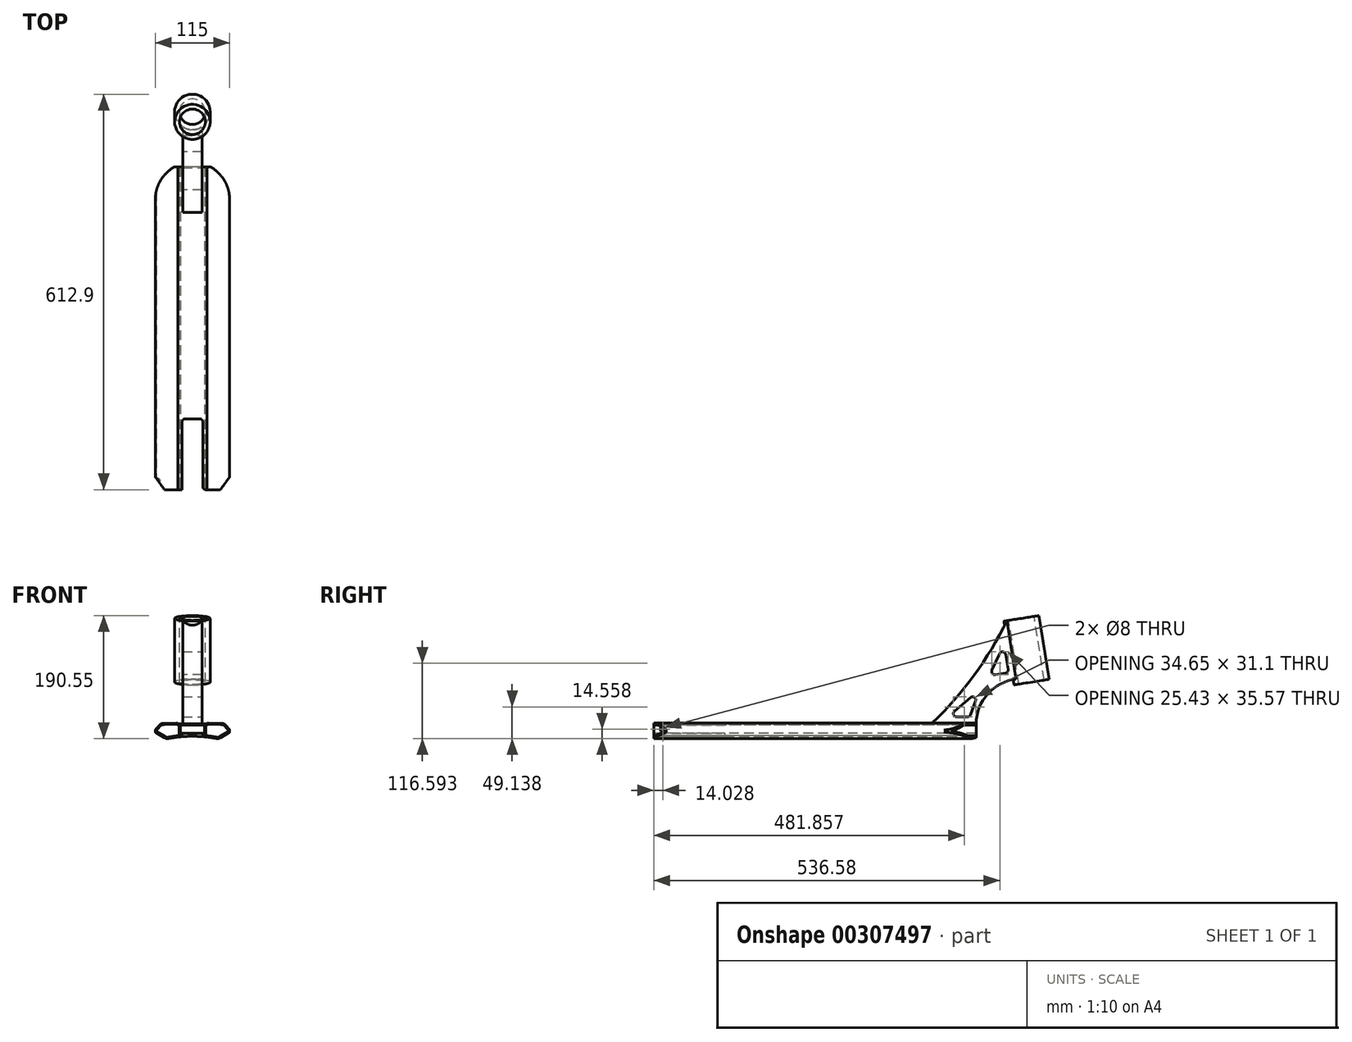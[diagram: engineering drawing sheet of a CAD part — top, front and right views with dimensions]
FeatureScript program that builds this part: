
annotation { "Feature Type Name" : "Feature", "Feature Type Description" : "" }
export const myFeature = defineFeature(function(context is Context, id is Id, definition is map)
    precondition{}
    {
        {
            var Q0;
            Q0=qCreatedBy(makeId("Front.planeOp"),FACE);
            var sketch = newSketch(context, id + "F0", { "sketchPlane" : qUnion([Q0])});
            skLineSegment(sketch, "E0", {"start": v(0, 0) * mm, "end": v(0, 16.32) * mm, "construction": true});
            skLineSegment(sketch, "E1.MirrorCS", {"start": v(-22.5, 0) * mm, "end": v(-22.5, 1.3) * mm});
            skLineSegment(sketch, "E2.MirrorCS", {"start": v(0, 0) * mm, "end": v(-22.5, 0) * mm});
            skLineSegment(sketch, "E3", {"start": v(-57.5, -9.13) * mm, "end": v(-57.5, -13.13) * mm});
            skLineSegment(sketch, "E4", {"start": v(-57.5, -13.13) * mm, "end": v(-40.18, -23.13) * mm});
            skLineSegment(sketch, "E5.MirrorCS", {"start": v(0, 0) * mm, "end": v(22.5, 0) * mm});
            skLineSegment(sketch, "E6.MirrorCS", {"start": v(22.5, 0) * mm, "end": v(22.5, 1.3) * mm});
            skLineSegment(sketch, "E7.MirrorCS", {"start": v(57.5, -9.13) * mm, "end": v(57.5, -13.13) * mm});
            skLineSegment(sketch, "E8.MirrorCS", {"start": v(57.5, -13.13) * mm, "end": v(40.18, -23.13) * mm});
            skArc(sketch, "E9", {"start": v(40.18, -23.13) * mm, "mid": v(0, -19.05) * mm, "end": v(-40.18, -23.13) * mm});
            skLineSegment(sketch, "E10", {"start": v(-57.5, -9.13) * mm, "end": v(-49.1, 0.87) * mm});
            skLineSegment(sketch, "E11", {"start": v(49.1, 0.87) * mm, "end": v(57.5, -9.13) * mm});
            skLineSegment(sketch, "E12", {"start": v(-49.1, 0.87) * mm, "end": v(-22.5, 1.3) * mm});
            skLineSegment(sketch, "E13", {"start": v(22.5, 1.3) * mm, "end": v(49.1, 0.87) * mm});
            skSolve(sketch);
        }
        {
            var Q0;
            Q0 = qSketchRegion(id + "F0", true);
            extrude(context, id + "F1", {"entities" : qUnion([Q0]), "endBound" : BoundingType.SYMMETRIC, "depth" : 500 * mm});
        }
        {
            var Q0;
            Q0=qCreatedBy(makeId("Front.planeOp"),FACE);
            var sketch = newSketch(context, id + "F2", { "sketchPlane" : qUnion([Q0])});
            skLineSegment(sketch, "E14.bottom", {"start": v(19, -14.63) * mm, "end": v(-19, -14.63) * mm});
            skLineSegment(sketch, "E14.top", {"start": v(19, -1.63) * mm, "end": v(-19, -1.63) * mm});
            skLineSegment(sketch, "E14.left", {"start": v(19, -14.63) * mm, "end": v(19, -1.63) * mm});
            skLineSegment(sketch, "E14.right", {"start": v(-19, -14.63) * mm, "end": v(-19, -1.63) * mm});
            skPoint(sketch, "E14.middle", {"position": v(0, -8.13) * mm});
            skSolve(sketch);
        }
        {
            var Q0;
            Q0 = qSketchRegion(id + "F2", true);
            extrude(context, id + "F3", {"entities" : qUnion([Q0]), "operationType" : NewBodyOperationType.REMOVE, "endBound" : BoundingType.SYMMETRIC, "oppositeDirection" : true, "depth" : 500 * mm});
        }
        {
            var Q0;
            Q0=makeQuery(id+"F1.opExtrude","SWEPT_EDGE",EDGE,{"disambiguationData":[OSD([sQuery(id+"F0.wireOp",EDGE,"E1.MirrorCS"),sQuery(id+"F0.wireOp",EDGE,"E12")])]});
            var Q1;
            Q1=makeQuery(id+"F1.opExtrude","SWEPT_EDGE",EDGE,{"disambiguationData":[OSD([sQuery(id+"F0.wireOp",EDGE,"E6.MirrorCS"),sQuery(id+"F0.wireOp",EDGE,"E13")])]});
            fillet(context, id + "F4", {"entities" : qUnion([Q0, Q1]), "radius" : 2 * mm, "tangentPropagation" : true, "allowEdgeOverflow" : false});
        }
        {
            var Q0;
            Q0=makeQuery(id+"F1.opExtrude","SWEPT_EDGE",EDGE,{"disambiguationData":[OSD([sQuery(id+"F0.wireOp",EDGE,"E10"),sQuery(id+"F0.wireOp",EDGE,"E12")])]});
            var Q1;
            Q1=makeQuery(id+"F1.opExtrude","SWEPT_EDGE",EDGE,{"disambiguationData":[OSD([sQuery(id+"F0.wireOp",EDGE,"E11"),sQuery(id+"F0.wireOp",EDGE,"E13")])]});
            var Q2;
            Q2=makeQuery(id+"F1.opExtrude","SWEPT_EDGE",EDGE,{"disambiguationData":[OSD([sQuery(id+"F0.wireOp",EDGE,"E8.MirrorCS"),sQuery(id+"F0.wireOp",EDGE,"E9")])]});
            var Q3;
            Q3=makeQuery(id+"F1.opExtrude","SWEPT_EDGE",EDGE,{"disambiguationData":[OSD([sQuery(id+"F0.wireOp",EDGE,"E4"),sQuery(id+"F0.wireOp",EDGE,"E9")])]});
            fillet(context, id + "F5", {"entities" : qUnion([Q0, Q1, Q2, Q3]), "radius" : 9 * mm, "tangentPropagation" : true, "allowEdgeOverflow" : false});
        }
        {
            var Q0;
            Q0=makeQuery(id+"F1.opExtrude","SWEPT_EDGE",EDGE,{"disambiguationData":[OSD([sQuery(id+"F0.wireOp",EDGE,"E3"),sQuery(id+"F0.wireOp",EDGE,"E10")])]});
            var Q1;
            Q1=makeQuery(id+"F1.opExtrude","SWEPT_EDGE",EDGE,{"disambiguationData":[OSD([sQuery(id+"F0.wireOp",EDGE,"E3"),sQuery(id+"F0.wireOp",EDGE,"E4")])]});
            var Q2;
            Q2=makeQuery(id+"F1.opExtrude","SWEPT_EDGE",EDGE,{"disambiguationData":[OSD([sQuery(id+"F0.wireOp",EDGE,"E7.MirrorCS"),sQuery(id+"F0.wireOp",EDGE,"E8.MirrorCS")])]});
            var Q3;
            Q3=makeQuery(id+"F1.opExtrude","SWEPT_EDGE",EDGE,{"disambiguationData":[OSD([sQuery(id+"F0.wireOp",EDGE,"E7.MirrorCS"),sQuery(id+"F0.wireOp",EDGE,"E11")])]});
            fillet(context, id + "F6", {"entities" : qUnion([Q0, Q1, Q2, Q3]), "radius" : 1 * mm, "tangentPropagation" : true, "allowEdgeOverflow" : false});
        }
        {
            var Q0;
            Q0=makeQuery(id+"F1.opExtrude","CAP_FACE",FACE,{"disambiguationData":[OSD([sQuery(id+"F0.wireOp",EDGE,"E1.MirrorCS"),sQuery(id+"F0.wireOp",EDGE,"E2.MirrorCS"),sQuery(id+"F0.wireOp",EDGE,"E3"),sQuery(id+"F0.wireOp",EDGE,"E4"),sQuery(id+"F0.wireOp",EDGE,"E5.MirrorCS"),sQuery(id+"F0.wireOp",EDGE,"E6.MirrorCS"),sQuery(id+"F0.wireOp",EDGE,"E7.MirrorCS"),sQuery(id+"F0.wireOp",EDGE,"E8.MirrorCS"),sQuery(id+"F0.wireOp",EDGE,"E9"),sQuery(id+"F0.wireOp",EDGE,"E10"),sQuery(id+"F0.wireOp",EDGE,"E11"),sQuery(id+"F0.wireOp",EDGE,"E12"),sQuery(id+"F0.wireOp",EDGE,"E13")])],"isStart":false});
            var sketch = newSketch(context, id + "F7", { "sketchPlane" : qUnion([Q0])});
            skLineSegment(sketch, "E15.0", {"start": v(-44.97, -1.06) * mm, "end": v(-24.36, -0.73) * mm});
            skArc(sketch, "E15.1", {"start": v(-44.97, -1.06) * mm, "mid": v(-47.87, -1.74) * mm, "end": v(-50.22, -3.56) * mm});
            skArc(sketch, "E15.2", {"start": v(-20.47, -18.1) * mm, "mid": v(-28.92, -19.13) * mm, "end": v(-37.3, -20.53) * mm});
            skArc(sketch, "E15.3", {"start": v(-42.1, -19.7) * mm, "mid": v(-39.78, -20.55) * mm, "end": v(-37.3, -20.53) * mm});
            skLineSegment(sketch, "E15.4", {"start": v(-55.66, -11.88) * mm, "end": v(-42.1, -19.7) * mm});
            skLineSegment(sketch, "E15.5", {"start": v(-55.93, -10.37) * mm, "end": v(-50.22, -3.56) * mm});
            skPoint(sketch, "E16.visualSharp", {"position": v(-56.7, -11.28) * mm});
            skArc(sketch, "E16.filletArc", {"start": v(-55.93, -10.37) * mm, "mid": v(-56.15, -11.19) * mm, "end": v(-55.66, -11.88) * mm});
            skArc(sketch, "E17", {"start": v(-24.36, -0.73) * mm, "mid": v(-23.22, -1.06) * mm, "end": v(-22.47, -1.98) * mm});
            skLineSegment(sketch, "E18", {"start": v(-22.47, -1.98) * mm, "end": v(-20.47, -1.95) * mm});
            skLineSegment(sketch, "E19", {"start": v(-20.47, -1.95) * mm, "end": v(-20.47, -18.1) * mm});
            skLineSegment(sketch, "E20", {"start": v(0, 0) * mm, "end": v(0, 9) * mm, "construction": true});
            skLineSegment(sketch, "E21.MirrorCS", {"start": v(22.47, -1.98) * mm, "end": v(20.47, -1.95) * mm});
            skArc(sketch, "E22.MirrorCS", {"start": v(24.36, -0.73) * mm, "mid": v(23.22, -1.06) * mm, "end": v(22.47, -1.98) * mm});
            skLineSegment(sketch, "E23.MirrorCS", {"start": v(44.97, -1.06) * mm, "end": v(24.36, -0.73) * mm});
            skArc(sketch, "E24.MirrorCS", {"start": v(44.97, -1.06) * mm, "mid": v(47.87, -1.74) * mm, "end": v(50.22, -3.56) * mm});
            skLineSegment(sketch, "E25.MirrorCS", {"start": v(55.93, -10.37) * mm, "end": v(50.22, -3.56) * mm});
            skArc(sketch, "E26.MirrorCS", {"start": v(55.93, -10.37) * mm, "mid": v(56.15, -11.19) * mm, "end": v(55.66, -11.88) * mm});
            skLineSegment(sketch, "E27.MirrorCS", {"start": v(55.66, -11.88) * mm, "end": v(42.1, -19.7) * mm});
            skArc(sketch, "E28.MirrorCS", {"start": v(42.1, -19.7) * mm, "mid": v(39.78, -20.55) * mm, "end": v(37.3, -20.53) * mm});
            skArc(sketch, "E29.MirrorCS", {"start": v(20.47, -18.1) * mm, "mid": v(28.92, -19.13) * mm, "end": v(37.3, -20.53) * mm});
            skLineSegment(sketch, "E30.MirrorCS", {"start": v(20.47, -1.95) * mm, "end": v(20.47, -18.1) * mm});
            skSolve(sketch);
        }
        {
            var Q0;
            Q0 = qSketchRegion(id + "F7", true);
            extrude(context, id + "F8", {"entities" : qUnion([Q0]), "operationType" : NewBodyOperationType.REMOVE, "endBound" : BoundingType.THROUGH_ALL, "oppositeDirection" : true, "depth" : 25 * mm, "hasSecondDirection" : true, "secondDirectionBound" : SecondDirectionBoundingType.THROUGH_ALL, "secondDirectionOppositeDirection" : false, "secondDirectionDepth" : 25 * mm});
        }
        {
            var Q0;
            Q0=qCreatedBy(makeId("Top.planeOp"),FACE);
            var sketch = newSketch(context, id + "F9", { "sketchPlane" : qUnion([Q0])});
            skArc(sketch, "E31", {"start": v(57.5, 200) * mm, "mid": v(0, 257.5) * mm, "end": v(-57.5, 200) * mm});
            skLineSegment(sketch, "E32", {"start": v(-57.5, 200) * mm, "end": v(-57.5, 280) * mm});
            skLineSegment(sketch, "E33", {"start": v(57.5, 200) * mm, "end": v(57.5, 280) * mm});
            skLineSegment(sketch, "E34", {"start": v(57.5, 280) * mm, "end": v(-57.5, 280) * mm});
            skSolve(sketch);
        }
        {
            var Q0;
            Q0=makeQuery(id+"F9.imprint","IMPRINT",FACE,{"disambiguationData":[TD([[makeQuery(id+"F9.imprint","IMPRINT",EDGE,{"derivedFrom":sQuery(id+"F9.wireOp",EDGE,"E31")}),-1.0]])]});
            extrude(context, id + "F10", {"entities" : qUnion([Q0]), "operationType" : NewBodyOperationType.REMOVE, "endBound" : BoundingType.THROUGH_ALL, "oppositeDirection" : true, "depth" : 25 * mm, "hasSecondDirection" : true, "secondDirectionBound" : SecondDirectionBoundingType.THROUGH_ALL, "secondDirectionOppositeDirection" : false, "secondDirectionDepth" : 25 * mm});
        }
        {
            var Q0;
            Q0=qCreatedBy(makeId("Top.planeOp"),FACE);
            var sketch = newSketch(context, id + "F11", { "sketchPlane" : qUnion([Q0])});
            skLineSegment(sketch, "E35", {"start": v(-68, -216) * mm, "end": v(-43.3, -250) * mm});
            skLineSegment(sketch, "E36", {"start": v(-43.3, -250) * mm, "end": v(-16, -250) * mm});
            skLineSegment(sketch, "E37", {"start": v(-16, -250) * mm, "end": v(-16, -140) * mm});
            skLineSegment(sketch, "E38", {"start": v(-16, -140) * mm, "end": v(16, -140) * mm});
            skLineSegment(sketch, "E39", {"start": v(16, -140) * mm, "end": v(16, -250) * mm});
            skLineSegment(sketch, "E40", {"start": v(16, -250) * mm, "end": v(43.3, -250) * mm});
            skLineSegment(sketch, "E41", {"start": v(43.3, -250) * mm, "end": v(68, -216) * mm});
            skLineSegment(sketch, "E42", {"start": v(68, -216) * mm, "end": v(68, -346) * mm});
            skLineSegment(sketch, "E43", {"start": v(68, -346) * mm, "end": v(-68, -346) * mm});
            skLineSegment(sketch, "E44", {"start": v(-68, -346) * mm, "end": v(-68, -216) * mm});
            skSolve(sketch);
        }
        {
            var Q0;
            Q0 = qSketchRegion(id + "F11", true);
            extrude(context, id + "F12", {"entities" : qUnion([Q0]), "operationType" : NewBodyOperationType.REMOVE, "endBound" : BoundingType.THROUGH_ALL, "depth" : 25 * mm, "hasSecondDirection" : true, "secondDirectionBound" : SecondDirectionBoundingType.THROUGH_ALL, "secondDirectionOppositeDirection" : true, "secondDirectionDepth" : 25 * mm});
        }
        {
            var Q0;
            {var subQ0=sQuery(id+"F11.wireOp",EDGE,"E37");var subQ1=sQuery(id+"F11.wireOp",EDGE,"E38");Q0=makeQuery(id+"F12.boolean.opBoolean","COPY",EDGE,{"disambiguationData":[TD([makeQuery(id+"F3.boolean.opBoolean","COPY",FACE,{"derivedFrom":makeQuery(id+"F3.opExtrude","SWEPT_FACE",FACE,{"disambiguationData":[OSD([sQuery(id+"F2.wireOp",EDGE,"E14.top")])]})})])],"derivedFrom":makeQuery(id+"F12.opExtrude","SWEPT_EDGE",EDGE,{"disambiguationData":[OSD([subQ0,subQ1])]})});}
            var Q1;
            {var subQ0=sQuery(id+"F11.wireOp",EDGE,"E38");var subQ1=sQuery(id+"F11.wireOp",EDGE,"E37");Q1=makeQuery(id+"F12.boolean.opBoolean","COPY",EDGE,{"disambiguationData":[TD([makeQuery(id+"F1.opExtrude","SWEPT_FACE",FACE,{"disambiguationData":[OSD([sQuery(id+"F0.wireOp",EDGE,"E9")])]})])],"derivedFrom":makeQuery(id+"F12.opExtrude","SWEPT_EDGE",EDGE,{"disambiguationData":[OSD([subQ1,subQ0])]})});}
            var Q2;
            {var subQ0=sQuery(id+"F11.wireOp",EDGE,"E38");var subQ1=sQuery(id+"F11.wireOp",EDGE,"E39");Q2=makeQuery(id+"F12.boolean.opBoolean","COPY",EDGE,{"disambiguationData":[TD([makeQuery(id+"F3.boolean.opBoolean","COPY",FACE,{"derivedFrom":makeQuery(id+"F3.opExtrude","SWEPT_FACE",FACE,{"disambiguationData":[OSD([sQuery(id+"F2.wireOp",EDGE,"E14.top")])]})})])],"derivedFrom":makeQuery(id+"F12.opExtrude","SWEPT_EDGE",EDGE,{"disambiguationData":[OSD([subQ0,subQ1])]})});}
            var Q3;
            {var subQ0=sQuery(id+"F11.wireOp",EDGE,"E38");var subQ1=sQuery(id+"F11.wireOp",EDGE,"E39");Q3=makeQuery(id+"F12.boolean.opBoolean","COPY",EDGE,{"disambiguationData":[TD([makeQuery(id+"F1.opExtrude","SWEPT_FACE",FACE,{"disambiguationData":[OSD([sQuery(id+"F0.wireOp",EDGE,"E9")])]})])],"derivedFrom":makeQuery(id+"F12.opExtrude","SWEPT_EDGE",EDGE,{"disambiguationData":[OSD([subQ0,subQ1])]})});}
            var Q4;
            {var subQ0=sQuery(id+"F0.wireOp",EDGE,"E9");var subQ1=sQuery(id+"F11.wireOp",EDGE,"E39");Q4=makeQuery(id+"F12.boolean.opBoolean","COPY",EDGE,{"disambiguationData":[TD([makeQuery(id+"F1.opExtrude","SWEPT_FACE",FACE,{"disambiguationData":[OSD([subQ0])]})])],"derivedFrom":makeQuery(id+"F12.opExtrude","SWEPT_EDGE",EDGE,{"disambiguationData":[OSD([subQ1,sQuery(id+"F11.wireOp",EDGE,"E40")])]})});}
            var Q5;
            {var subQ0=sQuery(id+"F0.wireOp",EDGE,"E9");var subQ1=sQuery(id+"F11.wireOp",EDGE,"E37");Q5=makeQuery(id+"F12.boolean.opBoolean","COPY",EDGE,{"disambiguationData":[TD([makeQuery(id+"F1.opExtrude","SWEPT_FACE",FACE,{"disambiguationData":[OSD([subQ0])]})])],"derivedFrom":makeQuery(id+"F12.opExtrude","SWEPT_EDGE",EDGE,{"disambiguationData":[OSD([sQuery(id+"F11.wireOp",EDGE,"E36"),subQ1])]})});}
            fillet(context, id + "F13", {"entities" : qUnion([Q0, Q1, Q2, Q3, Q4, Q5]), "radius" : 5 * mm, "tangentPropagation" : true, "allowEdgeOverflow" : false});
        }
        {
            var Q0;
            Q0=qCreatedBy(makeId("Right.planeOp"),FACE);
            var sketch = newSketch(context, id + "F14", { "sketchPlane" : qUnion([Q0])});
            skLineSegment(sketch, "E45", {"start": v(180, 0) * mm, "end": v(250, 0) * mm});
            skArc(sketch, "E46", {"start": v(180, 0) * mm, "mid": v(245.97, 74.66) * mm, "end": v(297.38, 160) * mm});
            skLineSegment(sketch, "E47", {"start": v(312.87, 62.2) * mm, "end": v(313.03, 61.23) * mm});
            skLineSegment(sketch, "E48", {"start": v(313.03, 61.23) * mm, "end": v(358.46, 68.43) * mm});
            skLineSegment(sketch, "E49", {"start": v(358.46, 68.43) * mm, "end": v(342.82, 167.2) * mm});
            skLineSegment(sketch, "E50", {"start": v(342.82, 167.2) * mm, "end": v(297.38, 160) * mm});
            skLineSegment(sketch, "E51", {"start": v(312.87, 62.2) * mm, "end": v(311.71, 69.5) * mm});
            skArc(sketch, "E52", {"start": v(311.71, 69.5) * mm, "mid": v(267.66, 46.48) * mm, "end": v(250, 0) * mm});
            skSolve(sketch);
        }
        {
            var Q0;
            Q0 = qSketchRegion(id + "F14", true);
            extrude(context, id + "F15", {"entities" : qUnion([Q0]), "operationType" : NewBodyOperationType.ADD, "endBound" : BoundingType.SYMMETRIC, "depth" : 30 * mm});
        }
        {
            var Q0;
            Q0=makeQuery(id+"F15.opExtrude","SWEPT_FACE",FACE,{"disambiguationData":[OSD([sQuery(id+"F14.wireOp",EDGE,"E50")])]});
            var sketch = newSketch(context, id + "F16", { "sketchPlane" : qUnion([Q0])});
            skCircle(sketch, "E53", {"center": v(-0.07, 341.75) * mm, "radius": 27.5 * mm});
            skSolve(sketch);
        }
        {
            var Q0;
            Q0 = qSketchRegion(id + "F16", true);
            var Q1;
            Q1=makeQuery(id+"F15.opExtrude","SWEPT_FACE",FACE,{"disambiguationData":[OSD([sQuery(id+"F14.wireOp",EDGE,"E48")])]});
            extrude(context, id + "F17", {"entities" : qUnion([Q0]), "operationType" : NewBodyOperationType.ADD, "endBound" : BoundingType.UP_TO_SURFACE, "oppositeDirection" : true, "endBoundEntityFace" : qUnion([Q1]), "depth" : 25 * mm});
        }
        {
            var Q0;
            Q0=makeQuery(id+"F17.boolean.opBoolean","MERGE",FACE,{"derivedFrom":[makeQuery(id+"F15.opExtrude","SWEPT_FACE",FACE,{"disambiguationData":[OSD([sQuery(id+"F14.wireOp",EDGE,"E50")])]}),makeQuery(id+"F17.opExtrude","CAP_FACE",FACE,{"disambiguationData":[OSD([sQuery(id+"F16.wireOp",EDGE,"E53")])],"isStart":true})]});
            var sketch = newSketch(context, id + "F18", { "sketchPlane" : qUnion([Q0])});
            skSolve(sketch);
        }
        {
            var Q0;
            Q0=makeQuery(id+"F18.imprint","IMPRINT",FACE,{"disambiguationData":[TD([[makeQuery(id+"F18.imprint","IMPRINT",EDGE,{"derivedFrom":makeQuery(id+"F17.opExtrude","CAP_EDGE",EDGE,{"disambiguationData":[OSD([sQuery(id+"F16.wireOp",EDGE,"E53")])],"isStart":true})}),1.0]])]});
            var sketch = newSketch(context, id + "F19", { "sketchPlane" : qUnion([Q0])});
            skPoint(sketch, "E54", {"position": v(-0.07, 341.75) * mm});
            skSolve(sketch);
        }
        {
            var Q0;
            Q0=sQuery(id+"F19.wireOp",VERTEX,"E54");
            var Q1;
            Q1=makeQuery(id+"F1.opExtrude","SWEPT_BODY",BODY,{"disambiguationData":[OSD([sQuery(id+"F0.wireOp",EDGE,"E1.MirrorCS"),sQuery(id+"F0.wireOp",EDGE,"E2.MirrorCS"),sQuery(id+"F0.wireOp",EDGE,"E3"),sQuery(id+"F0.wireOp",EDGE,"E4"),sQuery(id+"F0.wireOp",EDGE,"E5.MirrorCS"),sQuery(id+"F0.wireOp",EDGE,"E6.MirrorCS"),sQuery(id+"F0.wireOp",EDGE,"E7.MirrorCS"),sQuery(id+"F0.wireOp",EDGE,"E8.MirrorCS"),sQuery(id+"F0.wireOp",EDGE,"E9"),sQuery(id+"F0.wireOp",EDGE,"E10"),sQuery(id+"F0.wireOp",EDGE,"E11"),sQuery(id+"F0.wireOp",EDGE,"E12"),sQuery(id+"F0.wireOp",EDGE,"E13")])]});
            hole(context, id + "F20", {"style" : HoleStyle.SIMPLE, "endStyle" : HoleEndStyle.THROUGH, "holeDiameter" : 40 * mm, "isTappedThrough" : true, "tappedDepth" : 12 * mm, "tapClearance" : 3, "locations" : qUnion([Q0]), "scope" : qUnion([Q1])});
        }
        {
            var Q0;
            Q0=makeQuery(id+"F8.boolean.opBoolean","COPY",FACE,{"derivedFrom":makeQuery(id+"F8.opExtrude","SWEPT_FACE",FACE,{"disambiguationData":[OSD([sQuery(id+"F7.wireOp",EDGE,"E30.MirrorCS")])]})});
            var sketch = newSketch(context, id + "F21", { "sketchPlane" : qUnion([Q0])});
            skPoint(sketch, "E55", {"position": v(-235.97, -8.1) * mm});
            skSolve(sketch);
        }
        {
            var Q0;
            Q0=sQuery(id+"F21.wireOp",VERTEX,"E55");
            var Q1;
            Q1=makeQuery(id+"F1.opExtrude","SWEPT_BODY",BODY,{"disambiguationData":[OSD([sQuery(id+"F0.wireOp",EDGE,"E1.MirrorCS"),sQuery(id+"F0.wireOp",EDGE,"E2.MirrorCS"),sQuery(id+"F0.wireOp",EDGE,"E3"),sQuery(id+"F0.wireOp",EDGE,"E4"),sQuery(id+"F0.wireOp",EDGE,"E5.MirrorCS"),sQuery(id+"F0.wireOp",EDGE,"E6.MirrorCS"),sQuery(id+"F0.wireOp",EDGE,"E7.MirrorCS"),sQuery(id+"F0.wireOp",EDGE,"E8.MirrorCS"),sQuery(id+"F0.wireOp",EDGE,"E9"),sQuery(id+"F0.wireOp",EDGE,"E10"),sQuery(id+"F0.wireOp",EDGE,"E11"),sQuery(id+"F0.wireOp",EDGE,"E12"),sQuery(id+"F0.wireOp",EDGE,"E13")])]});
            hole(context, id + "F22", {"style" : HoleStyle.SIMPLE, "endStyle" : HoleEndStyle.THROUGH, "holeDiameter" : 8 * mm, "isTappedThrough" : true, "tappedDepth" : 12 * mm, "tapClearance" : 3, "locations" : qUnion([Q0]), "scope" : qUnion([Q1])});
        }
        {
            var Q0;
            Q0=makeQuery(id+"F15.opExtrude","CAP_FACE",FACE,{"disambiguationData":[OSD([sQuery(id+"F14.wireOp",EDGE,"E45"),sQuery(id+"F14.wireOp",EDGE,"E46"),sQuery(id+"F14.wireOp",EDGE,"E47"),sQuery(id+"F14.wireOp",EDGE,"E48"),sQuery(id+"F14.wireOp",EDGE,"E49"),sQuery(id+"F14.wireOp",EDGE,"E50"),sQuery(id+"F14.wireOp",EDGE,"E51"),sQuery(id+"F14.wireOp",EDGE,"E52")])],"isStart":false});
            var sketch = newSketch(context, id + "F23", { "sketchPlane" : qUnion([Q0])});
            skLineSegment(sketch, "E56", {"start": v(292.98, 123.87) * mm, "end": v(300.02, 79.42) * mm});
            skLineSegment(sketch, "E57", {"start": v(292.98, 123.87) * mm, "end": v(270.39, 74.73) * mm});
            skLineSegment(sketch, "E58", {"start": v(270.39, 74.73) * mm, "end": v(300.02, 79.42) * mm});
            skLineSegment(sketch, "E59", {"start": v(255.4, 53.22) * mm, "end": v(206, 10.94) * mm});
            skLineSegment(sketch, "E60", {"start": v(206, 10.94) * mm, "end": v(240, 10.94) * mm});
            skLineSegment(sketch, "E61", {"start": v(255.4, 53.22) * mm, "end": v(240, 10.94) * mm});
            skSolve(sketch);
        }
        {
            var Q0;
            Q0 = qSketchRegion(id + "F23", true);
            extrude(context, id + "F24", {"entities" : qUnion([Q0]), "operationType" : NewBodyOperationType.REMOVE, "endBound" : BoundingType.THROUGH_ALL, "oppositeDirection" : true, "depth" : 25 * mm});
        }
        {
            var Q0;
            Q0=makeQuery(id+"F24.boolean.opBoolean","COPY",EDGE,{"derivedFrom":makeQuery(id+"F24.opExtrude","SWEPT_EDGE",EDGE,{"disambiguationData":[OSD([sQuery(id+"F23.wireOp",EDGE,"E60"),sQuery(id+"F23.wireOp",EDGE,"E61")])]})});
            var Q1;
            Q1=makeQuery(id+"F24.boolean.opBoolean","COPY",EDGE,{"derivedFrom":makeQuery(id+"F24.opExtrude","SWEPT_EDGE",EDGE,{"disambiguationData":[OSD([sQuery(id+"F23.wireOp",EDGE,"E56"),sQuery(id+"F23.wireOp",EDGE,"E58")])]})});
            var Q2;
            Q2=makeQuery(id+"F24.boolean.opBoolean","COPY",EDGE,{"derivedFrom":makeQuery(id+"F24.opExtrude","SWEPT_EDGE",EDGE,{"disambiguationData":[OSD([sQuery(id+"F23.wireOp",EDGE,"E59"),sQuery(id+"F23.wireOp",EDGE,"E60")])]})});
            var Q3;
            Q3=makeQuery(id+"F24.boolean.opBoolean","COPY",EDGE,{"derivedFrom":makeQuery(id+"F24.opExtrude","SWEPT_EDGE",EDGE,{"disambiguationData":[OSD([sQuery(id+"F23.wireOp",EDGE,"E57"),sQuery(id+"F23.wireOp",EDGE,"E58")])]})});
            var Q4;
            Q4=makeQuery(id+"F24.boolean.opBoolean","COPY",EDGE,{"derivedFrom":makeQuery(id+"F24.opExtrude","SWEPT_EDGE",EDGE,{"disambiguationData":[OSD([sQuery(id+"F23.wireOp",EDGE,"E56"),sQuery(id+"F23.wireOp",EDGE,"E57")])]})});
            var Q5;
            Q5=makeQuery(id+"F24.boolean.opBoolean","COPY",EDGE,{"derivedFrom":makeQuery(id+"F24.opExtrude","SWEPT_EDGE",EDGE,{"disambiguationData":[OSD([sQuery(id+"F23.wireOp",EDGE,"E59"),sQuery(id+"F23.wireOp",EDGE,"E61")])]})});
            fillet(context, id + "F25", {"entities" : qUnion([Q0, Q1, Q2, Q3, Q4, Q5]), "radius" : 5 * mm, "tangentPropagation" : true, "allowEdgeOverflow" : false});
        }
    });
